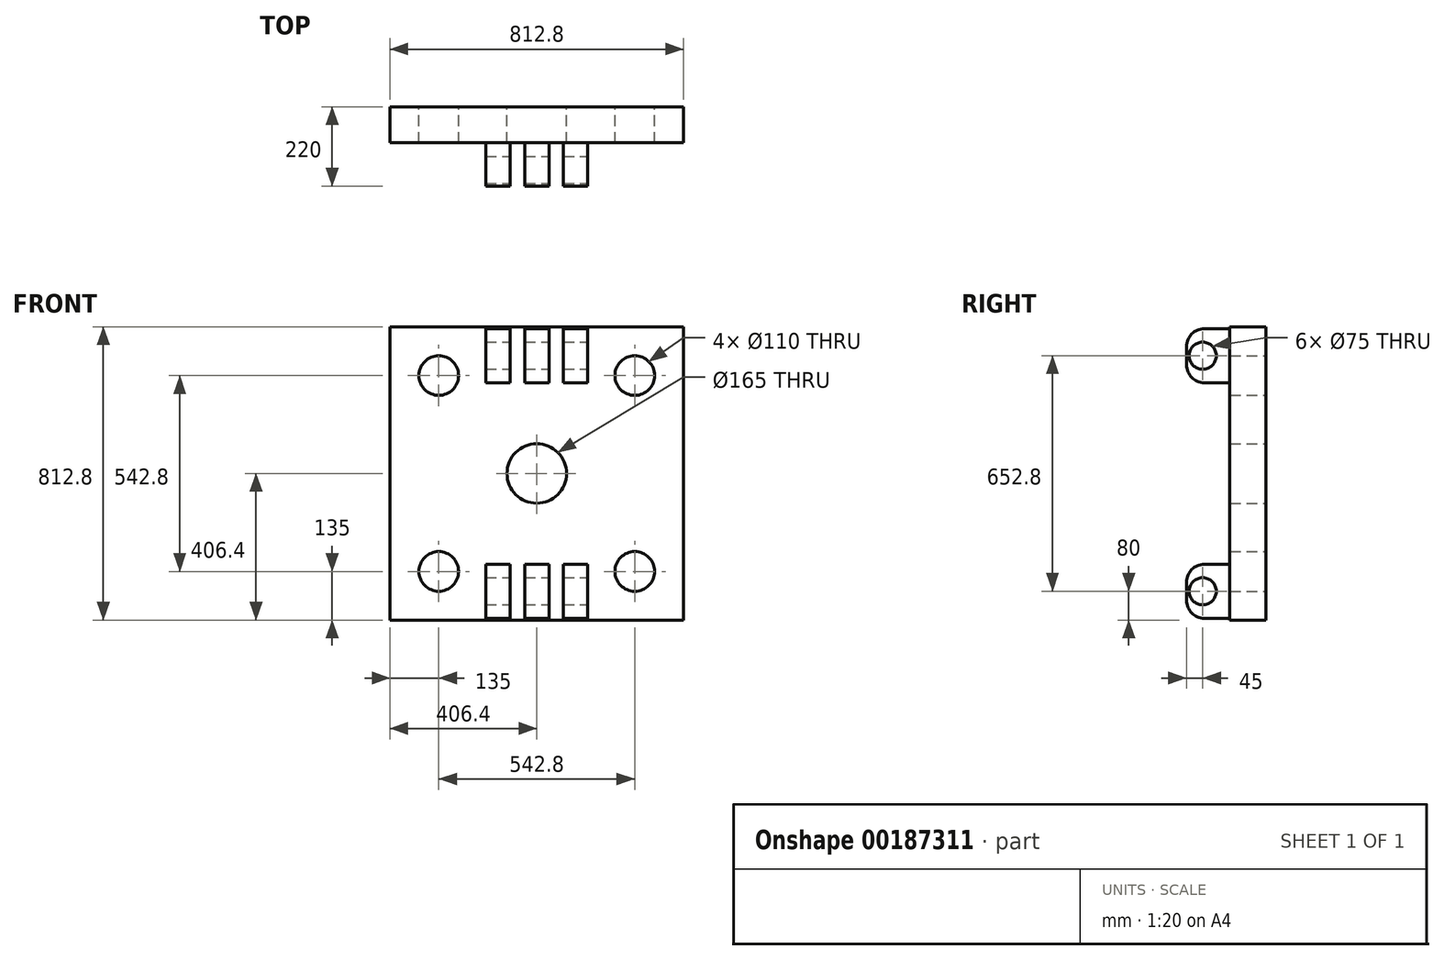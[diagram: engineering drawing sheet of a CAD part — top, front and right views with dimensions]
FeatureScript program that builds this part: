
annotation { "Feature Type Name" : "Feature", "Feature Type Description" : "" }
export const myFeature = defineFeature(function(context is Context, id is Id, definition is map)
    precondition{}
    {
        {
            var Q0;
            Q0=qCreatedBy(makeId("Front.planeOp"),FACE);
            var sketch = newSketch(context, id + "F0", { "sketchPlane" : qUnion([Q0])});
            skLineSegment(sketch, "E0.bottom", {"start": v(-406.4, -406.4) * mm, "end": v(406.4, -406.4) * mm});
            skLineSegment(sketch, "E0.top", {"start": v(-406.4, 406.4) * mm, "end": v(406.4, 406.4) * mm});
            skLineSegment(sketch, "E0.left", {"start": v(-406.4, -406.4) * mm, "end": v(-406.4, 406.4) * mm});
            skLineSegment(sketch, "E0.right", {"start": v(406.4, -406.4) * mm, "end": v(406.4, 406.4) * mm});
            skPoint(sketch, "E0.middle", {"position": v(0, 0) * mm});
            skLineSegment(sketch, "E1", {"start": v(-271.4, 435.08) * mm, "end": v(-271.4, -466.79) * mm, "construction": true});
            skLineSegment(sketch, "E2", {"start": v(271.4, 435.63) * mm, "end": v(271.4, -467.34) * mm, "construction": true});
            skLineSegment(sketch, "E3", {"start": v(-482.99, 271.4) * mm, "end": v(474.5, 271.4) * mm, "construction": true});
            skLineSegment(sketch, "E4", {"start": v(-470.32, -271.4) * mm, "end": v(478.3, -271.4) * mm, "construction": true});
            skCircle(sketch, "E5", {"center": v(-271.4, 271.4) * mm, "radius": 55 * mm});
            skLineSegment(sketch, "E6", {"start": v(-420.18, 0) * mm, "end": v(457.83, 0) * mm, "construction": true});
            skCircle(sketch, "E7.MirrorC", {"center": v(-271.4, -271.4) * mm, "radius": 55 * mm});
            skLineSegment(sketch, "E8", {"start": v(0, 436.93) * mm, "end": v(0, -451.52) * mm, "construction": true});
            skCircle(sketch, "E9.MirrorC", {"center": v(271.4, -271.4) * mm, "radius": 55 * mm});
            skCircle(sketch, "E10.MirrorC", {"center": v(271.4, 271.4) * mm, "radius": 55 * mm});
            skCircle(sketch, "E11", {"center": v(0, 0) * mm, "radius": 82.5 * mm});
            skSolve(sketch);
        }
        {
            var Q0;
            Q0=qSketchRegion(id+"F0",true);
            extrude(context, id + "F1", {"entities" : qUnion([Q0]), "depth" : 100 * mm});
        }
        {
            var Q0;
            Q0=makeQuery(id+"FbqTgrZJ77ltsDz_1.opFillet","SPLIT",FACE,{"disambiguationData":[OD(4.0)],"derivedFrom":makeQuery(id+"F1.opExtrude","CAP_FACE",FACE,{"disambiguationData":[OSD([sQuery(id+"F0.wireOp",EDGE,"E0.bottom"),sQuery(id+"F0.wireOp",EDGE,"E0.top"),sQuery(id+"F0.wireOp",EDGE,"E0.left"),sQuery(id+"F0.wireOp",EDGE,"E0.right"),sQuery(id+"F0.wireOp",EDGE,"E5"),sQuery(id+"F0.wireOp",EDGE,"E7.MirrorC"),sQuery(id+"F0.wireOp",EDGE,"E9.MirrorC"),sQuery(id+"F0.wireOp",EDGE,"E10.MirrorC"),sQuery(id+"F0.wireOp",EDGE,"E11")])],"isStart":false})});
            var sketch = newSketch(context, id + "F2", { "sketchPlane" : qUnion([Q0])});
            skLineSegment(sketch, "E12.left", {"start": v(-73.8, 401.4) * mm, "end": v(-73.8, 251.4) * mm});
            skLineSegment(sketch, "E12.right", {"start": v(-33.8, 401.4) * mm, "end": v(-33.8, 251.4) * mm});
            skLineSegment(sketch, "E13.left", {"start": v(33.8, 401.4) * mm, "end": v(33.8, 251.4) * mm});
            skLineSegment(sketch, "E13.right", {"start": v(73.8, 401.4) * mm, "end": v(73.8, 251.4) * mm});
            skLineSegment(sketch, "E14.left", {"start": v(141.4, 401.4) * mm, "end": v(141.4, 251.4) * mm});
            skLineSegment(sketch, "E15", {"start": v(33.8, 401.4) * mm, "end": v(-33.8, 401.4) * mm, "construction": true});
            skLineSegment(sketch, "E16", {"start": v(73.8, 401.4) * mm, "end": v(141.4, 401.4) * mm, "construction": true});
            skLineSegment(sketch, "E17", {"start": v(-406.4, 0) * mm, "end": v(406.4, 0) * mm, "construction": true});
            skLineSegment(sketch, "E18.right", {"start": v(-141.4, 401.4) * mm, "end": v(-141.4, 251.4) * mm});
            skLineSegment(sketch, "E19", {"start": v(-73.8, 401.4) * mm, "end": v(-141.4, 401.4) * mm, "construction": true});
            skLineSegment(sketch, "E20", {"start": v(141.4, 251.4) * mm, "end": v(73.8, 251.4) * mm});
            skLineSegment(sketch, "E21", {"start": v(141.4, 401.4) * mm, "end": v(73.8, 401.4) * mm});
            skLineSegment(sketch, "E22", {"start": v(33.8, 401.4) * mm, "end": v(-33.8, 401.4) * mm});
            skLineSegment(sketch, "E23", {"start": v(-73.8, 401.4) * mm, "end": v(-141.4, 401.4) * mm});
            skLineSegment(sketch, "E24", {"start": v(-141.4, 251.4) * mm, "end": v(-73.8, 251.4) * mm});
            skLineSegment(sketch, "E25", {"start": v(-33.8, 251.4) * mm, "end": v(33.8, 251.4) * mm});
            skLineSegment(sketch, "E26.MirrorCS", {"start": v(141.4, -401.4) * mm, "end": v(73.8, -401.4) * mm});
            skLineSegment(sketch, "E27.MirrorCS", {"start": v(-73.8, -401.4) * mm, "end": v(-141.4, -401.4) * mm});
            skLineSegment(sketch, "E28.MirrorCS", {"start": v(33.8, -401.4) * mm, "end": v(-33.8, -401.4) * mm});
            skLineSegment(sketch, "E29.MirrorCS", {"start": v(-141.4, -251.4) * mm, "end": v(-73.8, -251.4) * mm});
            skLineSegment(sketch, "E30.MirrorCS", {"start": v(73.8, -401.4) * mm, "end": v(73.8, -251.4) * mm});
            skLineSegment(sketch, "E31.MirrorCS", {"start": v(-73.8, -401.4) * mm, "end": v(-73.8, -251.4) * mm});
            skLineSegment(sketch, "E32.MirrorCS", {"start": v(33.8, -401.4) * mm, "end": v(33.8, -251.4) * mm});
            skLineSegment(sketch, "E33.MirrorCS", {"start": v(141.4, -251.4) * mm, "end": v(73.8, -251.4) * mm});
            skLineSegment(sketch, "E34.MirrorCS", {"start": v(-33.8, -401.4) * mm, "end": v(-33.8, -251.4) * mm});
            skLineSegment(sketch, "E35.MirrorCS", {"start": v(33.8, -401.4) * mm, "end": v(-33.8, -401.4) * mm, "construction": true});
            skLineSegment(sketch, "E36.MirrorCS", {"start": v(-73.8, -401.4) * mm, "end": v(-141.4, -401.4) * mm, "construction": true});
            skLineSegment(sketch, "E37.MirrorCS", {"start": v(73.8, -401.4) * mm, "end": v(141.4, -401.4) * mm, "construction": true});
            skLineSegment(sketch, "E38.MirrorCS", {"start": v(141.4, -401.4) * mm, "end": v(141.4, -251.4) * mm});
            skLineSegment(sketch, "E39.MirrorCS", {"start": v(-33.8, -251.4) * mm, "end": v(33.8, -251.4) * mm});
            skLineSegment(sketch, "E40.MirrorCS", {"start": v(-141.4, -401.4) * mm, "end": v(-141.4, -251.4) * mm});
            skSolve(sketch);
        }
        {
            var Q0;
            Q0=qSketchRegion(id+"F2",true);
            extrude(context, id + "F3", {"entities" : qUnion([Q0]), "operationType" : NewBodyOperationType.ADD, "depth" : 120 * mm});
        }
        {
            var Q0;
            Q0=makeQuery(id+"F3.opExtrude","CAP_EDGE",EDGE,{"disambiguationData":[OSD([sQuery(id+"F2.wireOp",EDGE,"E26.MirrorCS")])],"isStart":false});
            var Q1;
            Q1=makeQuery(id+"F3.opExtrude","CAP_EDGE",EDGE,{"disambiguationData":[OSD([sQuery(id+"F2.wireOp",EDGE,"E28.MirrorCS")])],"isStart":false});
            var Q2;
            Q2=makeQuery(id+"F3.opExtrude","CAP_EDGE",EDGE,{"disambiguationData":[OSD([sQuery(id+"F2.wireOp",EDGE,"E27.MirrorCS")])],"isStart":false});
            var Q3;
            Q3=makeQuery(id+"F3.opExtrude","CAP_EDGE",EDGE,{"disambiguationData":[OSD([sQuery(id+"F2.wireOp",EDGE,"E29.MirrorCS")])],"isStart":false});
            var Q4;
            Q4=makeQuery(id+"F3.opExtrude","CAP_EDGE",EDGE,{"disambiguationData":[OSD([sQuery(id+"F2.wireOp",EDGE,"E39.MirrorCS")])],"isStart":false});
            var Q5;
            Q5=makeQuery(id+"F3.opExtrude","CAP_EDGE",EDGE,{"disambiguationData":[OSD([sQuery(id+"F2.wireOp",EDGE,"E33.MirrorCS")])],"isStart":false});
            var Q6;
            Q6=makeQuery(id+"F3.opExtrude","CAP_EDGE",EDGE,{"disambiguationData":[OSD([sQuery(id+"F2.wireOp",EDGE,"E20")])],"isStart":false});
            var Q7;
            Q7=makeQuery(id+"F3.opExtrude","CAP_EDGE",EDGE,{"disambiguationData":[OSD([sQuery(id+"F2.wireOp",EDGE,"E21")])],"isStart":false});
            var Q8;
            Q8=makeQuery(id+"F3.opExtrude","CAP_EDGE",EDGE,{"disambiguationData":[OSD([sQuery(id+"F2.wireOp",EDGE,"E25")])],"isStart":false});
            var Q9;
            Q9=makeQuery(id+"F3.opExtrude","CAP_EDGE",EDGE,{"disambiguationData":[OSD([sQuery(id+"F2.wireOp",EDGE,"E22")])],"isStart":false});
            var Q10;
            Q10=makeQuery(id+"F3.opExtrude","CAP_EDGE",EDGE,{"disambiguationData":[OSD([sQuery(id+"F2.wireOp",EDGE,"E23")])],"isStart":false});
            var Q11;
            Q11=makeQuery(id+"F3.opExtrude","CAP_EDGE",EDGE,{"disambiguationData":[OSD([sQuery(id+"F2.wireOp",EDGE,"E24")])],"isStart":false});
            fillet(context, id + "F4", {"entities" : qUnion([Q0, Q1, Q2, Q3, Q4, Q5, Q6, Q7, Q8, Q9, Q10, Q11]), "radius" : 50 * mm, "tangentPropagation" : true, "allowEdgeOverflow" : false});
        }
        {
            var Q0;
            Q0=makeQuery(id+"F3.opExtrude","SWEPT_FACE",FACE,{"disambiguationData":[OSD([sQuery(id+"F2.wireOp",EDGE,"E38.MirrorCS")])]});
            var sketch = newSketch(context, id + "F5", { "sketchPlane" : qUnion([Q0])});
            skCircle(sketch, "E41", {"center": v(-175, -326.4) * mm, "radius": 37.5 * mm});
            skPoint(sketch, "E42", {"position": v(-220, -326.4) * mm});
            skCircle(sketch, "E43", {"center": v(-175, 326.4) * mm, "radius": 37.5 * mm});
            skSolve(sketch);
        }
        {
            var Q0;
            Q0 = qSketchRegion(id + "F5", true);
            extrude(context, id + "F6", {"entities" : qUnion([Q0]), "operationType" : NewBodyOperationType.REMOVE, "endBound" : BoundingType.THROUGH_ALL, "oppositeDirection" : true, "depth" : 25 * mm});
        }
    });
